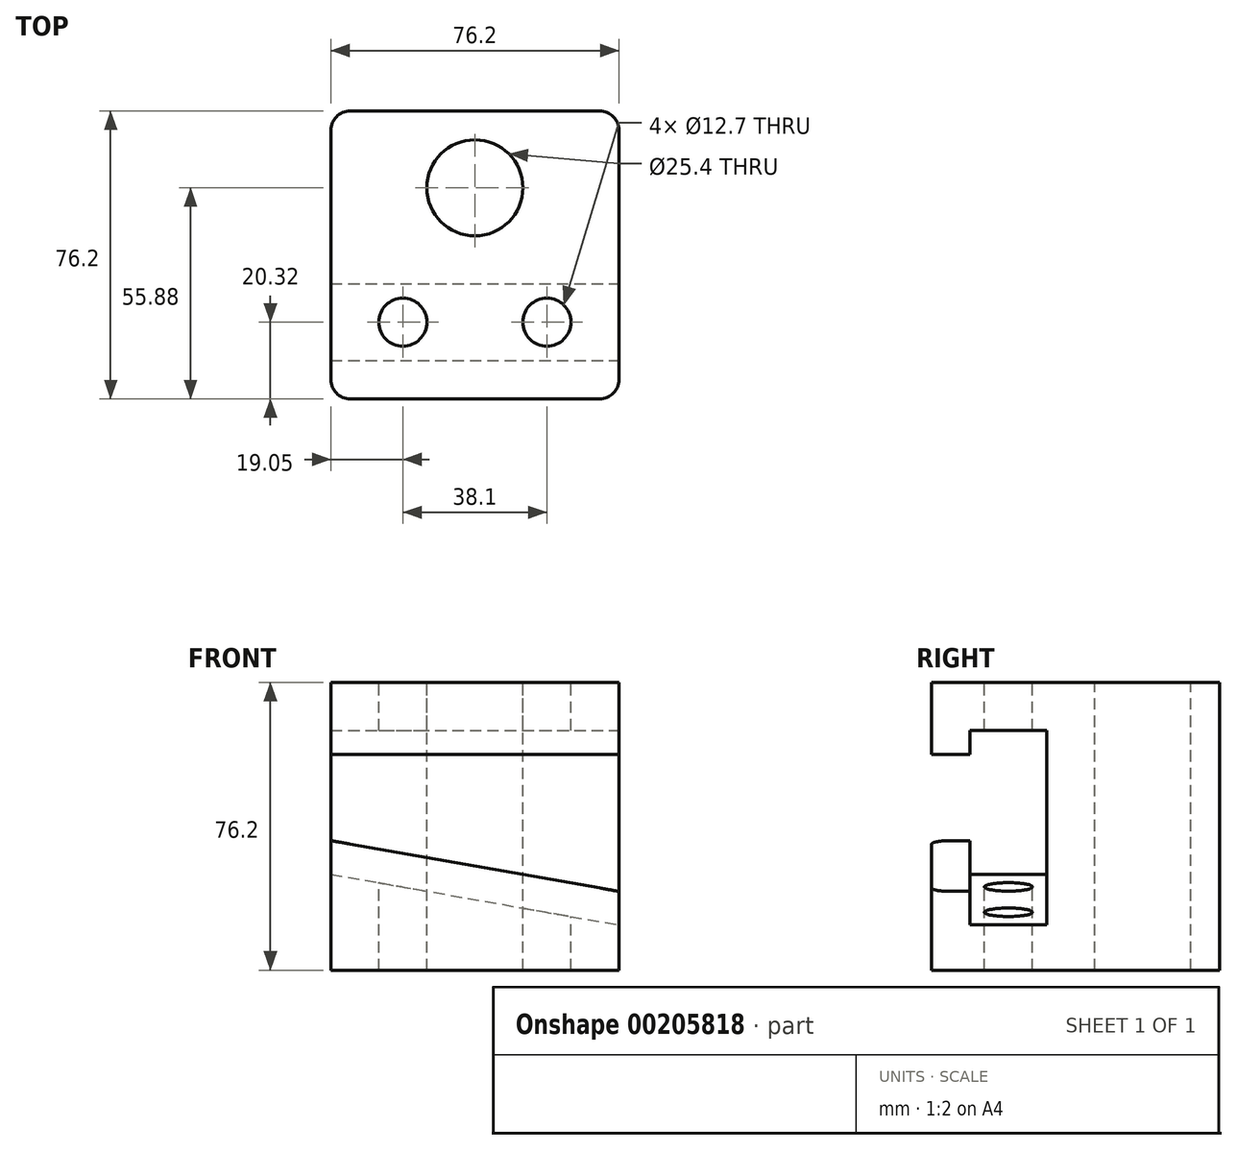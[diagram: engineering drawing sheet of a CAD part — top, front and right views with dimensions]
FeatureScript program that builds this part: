
annotation { "Feature Type Name" : "Feature", "Feature Type Description" : "" }
export const myFeature = defineFeature(function(context is Context, id is Id, definition is map)
    precondition{}
    {
        {
            var Q0;
            Q0=qCreatedBy(makeId("Top.planeOp"),FACE);
            var sketch = newSketch(context, id + "F0", { "sketchPlane" : qUnion([Q0])});
            skLineSegment(sketch, "E0.bottom", {"start": v(38.1, -38.1) * mm, "end": v(-38.1, -38.1) * mm});
            skLineSegment(sketch, "E0.top", {"start": v(38.1, 38.1) * mm, "end": v(-38.1, 38.1) * mm});
            skLineSegment(sketch, "E0.left", {"start": v(38.1, -38.1) * mm, "end": v(38.1, 38.1) * mm});
            skLineSegment(sketch, "E0.right", {"start": v(-38.1, -38.1) * mm, "end": v(-38.1, 38.1) * mm});
            skPoint(sketch, "E0.middle", {"position": v(0, 0) * mm});
            skSolve(sketch);
        }
        {
            var Q0;
            Q0=makeQuery(id+"F0.imprint","IMPRINT",FACE,{"disambiguationData":[TD([[makeQuery(id+"F0.imprint","IMPRINT",EDGE,{"derivedFrom":sQuery(id+"F0.wireOp",EDGE,"E0.bottom")}),-1.0]])]});
            extrude(context, id + "F1", {"entities" : qUnion([Q0]), "depth" : 76.2 * mm});
        }
        {
            var Q0;
            Q0=makeQuery(id+"F1.opExtrude","SWEPT_FACE",FACE,{"disambiguationData":[OSD([sQuery(id+"F0.wireOp",EDGE,"E0.right")])]});
            var sketch = newSketch(context, id + "F2", { "sketchPlane" : qUnion([Q0])});
            skLineSegment(sketch, "E1", {"start": v(38.1, 57.15) * mm, "end": v(27.94, 57.15) * mm});
            skLineSegment(sketch, "E2", {"start": v(27.94, 57.15) * mm, "end": v(27.94, 63.5) * mm});
            skLineSegment(sketch, "E3", {"start": v(27.94, 63.5) * mm, "end": v(7.62, 63.5) * mm});
            skLineSegment(sketch, "E4", {"start": v(7.62, 63.5) * mm, "end": v(7.62, 25.4) * mm});
            skLineSegment(sketch, "E5", {"start": v(7.62, 25.4) * mm, "end": v(27.94, 25.4) * mm});
            skLineSegment(sketch, "E6", {"start": v(27.94, 25.4) * mm, "end": v(27.94, 34.3) * mm});
            skLineSegment(sketch, "E7", {"start": v(27.94, 34.3) * mm, "end": v(38.1, 34.3) * mm});
            skLineSegment(sketch, "E8", {"start": v(38.1, 34.3) * mm, "end": v(38.1, 57.15) * mm});
            skSolve(sketch);
        }
        {
            var Q0;
            Q0=makeQuery(id+"F1.opExtrude","SWEPT_FACE",FACE,{"disambiguationData":[OSD([sQuery(id+"F0.wireOp",EDGE,"E0.bottom")])]});
            var sketch = newSketch(context, id + "F3", { "sketchPlane" : qUnion([Q0])});
            skPoint(sketch, "E9.0", {"position": v(-38.1, 34.3) * mm});
            skLineSegment(sketch, "E10", {"start": v(-38.1, 34.3) * mm, "end": v(38.1, 20.85) * mm});
            skSolve(sketch);
        }
        {
            var Q0;
            Q0=makeQuery(id+"F1.opExtrude","SWEPT_FACE",FACE,{"disambiguationData":[OSD([sQuery(id+"F0.wireOp",EDGE,"E0.left")])]});
            var sketch = newSketch(context, id + "F4", { "sketchPlane" : qUnion([Q0])});
            skLineSegment(sketch, "E11", {"start": v(-38.1, 57.15) * mm, "end": v(-27.94, 57.15) * mm});
            skLineSegment(sketch, "E12", {"start": v(-27.94, 57.15) * mm, "end": v(-27.94, 63.5) * mm});
            skLineSegment(sketch, "E13", {"start": v(-27.94, 63.5) * mm, "end": v(-7.62, 63.5) * mm});
            skLineSegment(sketch, "E14", {"start": v(-7.62, 63.5) * mm, "end": v(-7.62, 11.96) * mm});
            skLineSegment(sketch, "E15", {"start": v(-7.62, 11.96) * mm, "end": v(-27.94, 11.96) * mm});
            skLineSegment(sketch, "E16", {"start": v(-27.94, 11.96) * mm, "end": v(-27.94, 20.85) * mm});
            skLineSegment(sketch, "E17", {"start": v(-27.94, 20.85) * mm, "end": v(-38.1, 20.85) * mm});
            skLineSegment(sketch, "E18", {"start": v(-38.1, 57.15) * mm, "end": v(-38.1, 20.85) * mm});
            skSolve(sketch);
        }
        {
            var Q1;
            Q1=makeQuery(id+"F2.imprint","IMPRINT",FACE,{"disambiguationData":[TD([[makeQuery(id+"F2.imprint","IMPRINT",EDGE,{"derivedFrom":sQuery(id+"F2.wireOp",EDGE,"E1")}),1.0]])]});
            var Q2;
            Q2=makeQuery(id+"F4.imprint","IMPRINT",FACE,{"disambiguationData":[TD([[makeQuery(id+"F4.imprint","IMPRINT",EDGE,{"derivedFrom":sQuery(id+"F4.wireOp",EDGE,"E11")}),-1.0]])]});
            loft(context, id + "F5", {"operationType" : NewBodyOperationType.REMOVE, "sheetProfilesArray" : [{ "sheetProfileEntities" : qUnion([Q1]) }, { "sheetProfileEntities" : qUnion([Q2]) }]});
        }
        {
            var Q0;
            Q0=makeQuery(id+"F1.opExtrude","CAP_FACE",FACE,{"disambiguationData":[OSD([sQuery(id+"F0.wireOp",EDGE,"E0.bottom"),sQuery(id+"F0.wireOp",EDGE,"E0.top"),sQuery(id+"F0.wireOp",EDGE,"E0.left"),sQuery(id+"F0.wireOp",EDGE,"E0.right")])],"isStart":false});
            var sketch = newSketch(context, id + "F6", { "sketchPlane" : qUnion([Q0])});
            skCircle(sketch, "E19", {"center": v(-19.05, -17.78) * mm, "radius": 6.35 * mm});
            skCircle(sketch, "E20", {"center": v(19.05, -17.78) * mm, "radius": 6.35 * mm});
            skCircle(sketch, "E21", {"center": v(0, 17.78) * mm, "radius": 12.7 * mm});
            skSolve(sketch);
        }
        {
            var Q0;
            Q0 = qSketchRegion(id + "F6", true);
            extrude(context, id + "F7", {"entities" : qUnion([Q0]), "operationType" : NewBodyOperationType.REMOVE, "endBound" : BoundingType.THROUGH_ALL, "oppositeDirection" : true, "depth" : 25.4 * mm});
        }
        {
            var Q0;
            {var subQ0=sQuery(id+"F0.wireOp",EDGE,"E0.bottom");var subQ1=sQuery(id+"F0.wireOp",EDGE,"E0.right");Q0=makeQuery(id+"FRdKwFUBWTaQmFD_1.boolean.opBoolean","SPLIT",EDGE,{"disambiguationData":[TD([makeQuery(id+"FRdKwFUBWTaQmFD_1.opSweep","SWEPT_FACE",FACE,{"disambiguationData":[OSD([sQuery(id+"F2.wireOp",EDGE,"E1"),sQuery(id+"F3.wireOp",EDGE,"E10")])]})])],"derivedFrom":makeQuery(id+"F1.opExtrude","SWEPT_EDGE",EDGE,{"disambiguationData":[OSD([subQ0,subQ1])]})});}
            var Q1;
            {var subQ0=sQuery(id+"F0.wireOp",EDGE,"E0.bottom");var subQ1=sQuery(id+"F0.wireOp",EDGE,"E0.right");Q1=makeQuery(id+"FRdKwFUBWTaQmFD_1.boolean.opBoolean","SPLIT",EDGE,{"disambiguationData":[TD([makeQuery(id+"FRdKwFUBWTaQmFD_1.opSweep","SWEPT_FACE",FACE,{"disambiguationData":[OSD([sQuery(id+"F2.wireOp",EDGE,"E7"),sQuery(id+"F3.wireOp",EDGE,"E10")])]})])],"derivedFrom":makeQuery(id+"F1.opExtrude","SWEPT_EDGE",EDGE,{"disambiguationData":[OSD([subQ0,subQ1])]})});}
            var Q2;
            {var subQ0=sQuery(id+"F0.wireOp",EDGE,"E0.bottom");var subQ1=sQuery(id+"F0.wireOp",EDGE,"E0.left");Q2=makeQuery(id+"FRdKwFUBWTaQmFD_1.boolean.opBoolean","SPLIT",EDGE,{"disambiguationData":[TD([makeQuery(id+"FRdKwFUBWTaQmFD_1.opSweep","SWEPT_FACE",FACE,{"disambiguationData":[OSD([sQuery(id+"F2.wireOp",EDGE,"E7"),sQuery(id+"F3.wireOp",EDGE,"E10")])]})])],"derivedFrom":makeQuery(id+"F1.opExtrude","SWEPT_EDGE",EDGE,{"disambiguationData":[OSD([subQ0,subQ1])]})});}
            var Q3;
            {var subQ0=sQuery(id+"F0.wireOp",EDGE,"E0.bottom");var subQ1=sQuery(id+"F0.wireOp",EDGE,"E0.left");Q3=makeQuery(id+"FRdKwFUBWTaQmFD_1.boolean.opBoolean","SPLIT",EDGE,{"disambiguationData":[TD([makeQuery(id+"FRdKwFUBWTaQmFD_1.opSweep","SWEPT_FACE",FACE,{"disambiguationData":[OSD([sQuery(id+"F2.wireOp",EDGE,"E1"),sQuery(id+"F3.wireOp",EDGE,"E10")])]})])],"derivedFrom":makeQuery(id+"F1.opExtrude","SWEPT_EDGE",EDGE,{"disambiguationData":[OSD([subQ0,subQ1])]})});}
            var Q4;
            Q4=makeQuery(id+"F1.opExtrude","SWEPT_EDGE",EDGE,{"disambiguationData":[OSD([sQuery(id+"F0.wireOp",EDGE,"E0.top"),sQuery(id+"F0.wireOp",EDGE,"E0.left")])]});
            var Q5;
            Q5=makeQuery(id+"F1.opExtrude","SWEPT_EDGE",EDGE,{"disambiguationData":[OSD([sQuery(id+"F0.wireOp",EDGE,"E0.top"),sQuery(id+"F0.wireOp",EDGE,"E0.right")])]});
            fillet(context, id + "F8", {"entities" : qUnion([Q0, Q1, Q2, Q3, Q4, Q5]), "radius" : 5.08 * mm, "tangentPropagation" : true, "allowEdgeOverflow" : false});
        }
    });
